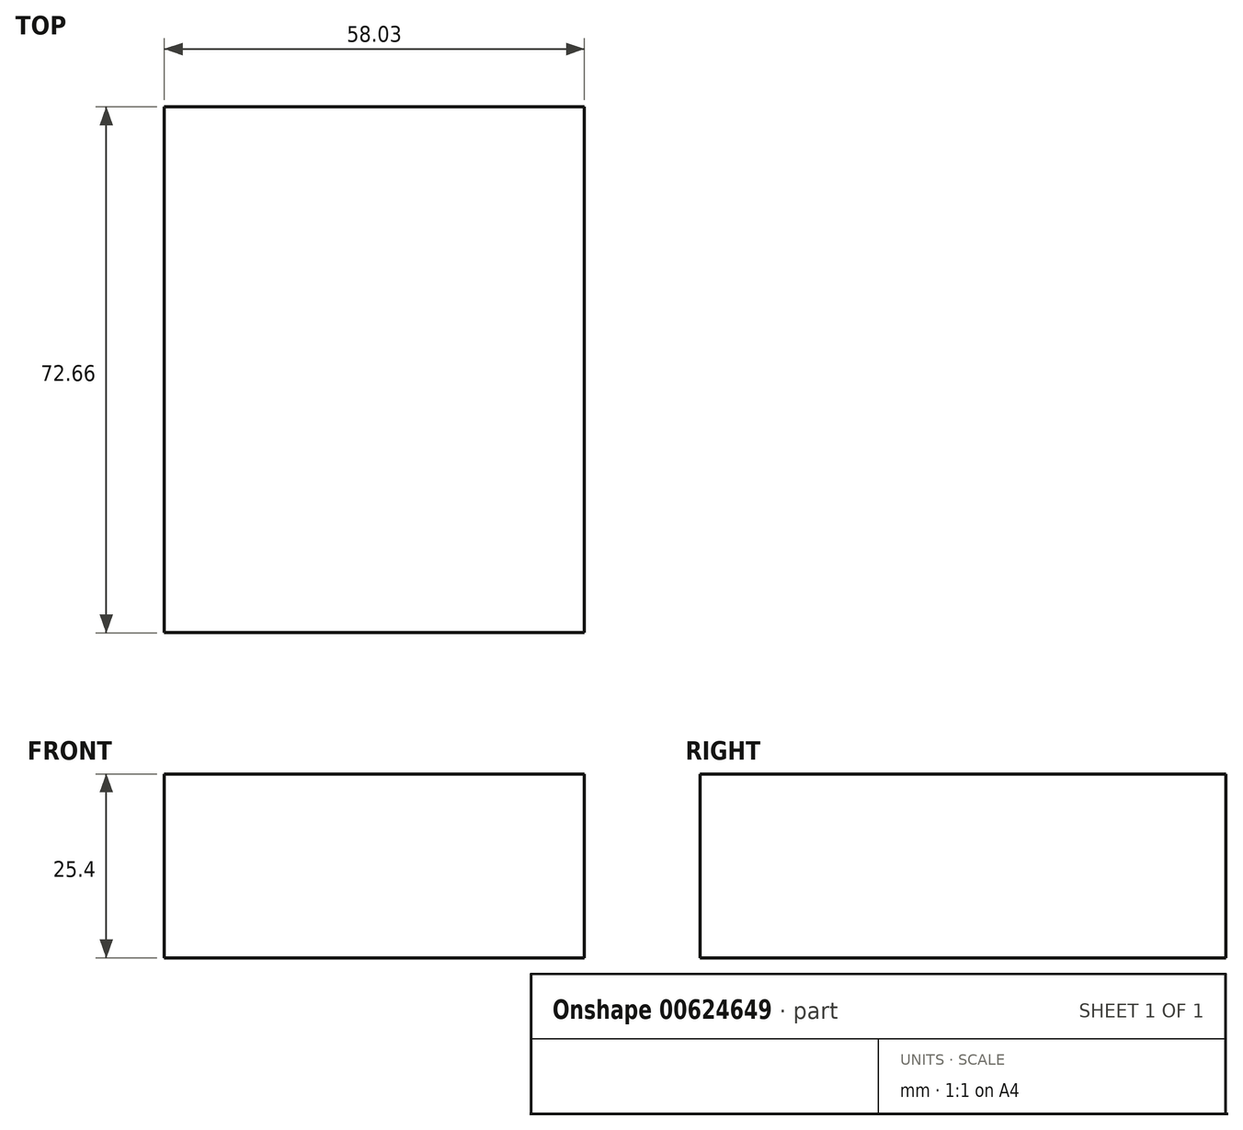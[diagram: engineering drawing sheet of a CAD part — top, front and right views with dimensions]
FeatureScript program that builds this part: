
annotation { "Feature Type Name" : "Feature", "Feature Type Description" : "" }
export const myFeature = defineFeature(function(context is Context, id is Id, definition is map)
    precondition{}
    {
        {
            var Q0;
            Q0=qCreatedBy(makeId("Top.planeOp"),FACE);
            var sketch = newSketch(context, id + "F0", { "sketchPlane" : qUnion([Q0])});
            skLineSegment(sketch, "E0.bottom", {"start": v(29.27, -32.12) * mm, "end": v(-28.76, -32.12) * mm});
            skLineSegment(sketch, "E0.top", {"start": v(29.27, 40.54) * mm, "end": v(-28.76, 40.54) * mm});
            skLineSegment(sketch, "E0.left", {"start": v(29.27, -32.12) * mm, "end": v(29.27, 40.54) * mm});
            skLineSegment(sketch, "E0.right", {"start": v(-28.76, -32.12) * mm, "end": v(-28.76, 40.54) * mm});
            skSolve(sketch);
        }
        {
            var Q0;
            Q0=makeQuery(id+"F0.imprint","IMPRINT",FACE,{"disambiguationData":[TD([[makeQuery(id+"F0.imprint","IMPRINT",EDGE,{"derivedFrom":sQuery(id+"F0.wireOp",EDGE,"E0.bottom")}),-1.0]])]});
            var Q1;
            Q1=sQuery(id+"F0.wireOp",EDGE,"E0.bottom");
            extrude(context, id + "F1", {"entities" : qUnion([Q0]), "surfaceEntities" : qUnion([Q1]), "depth" : 25.4 * mm, "offsetDistance" : 25.4 * mm});
        }
    });
